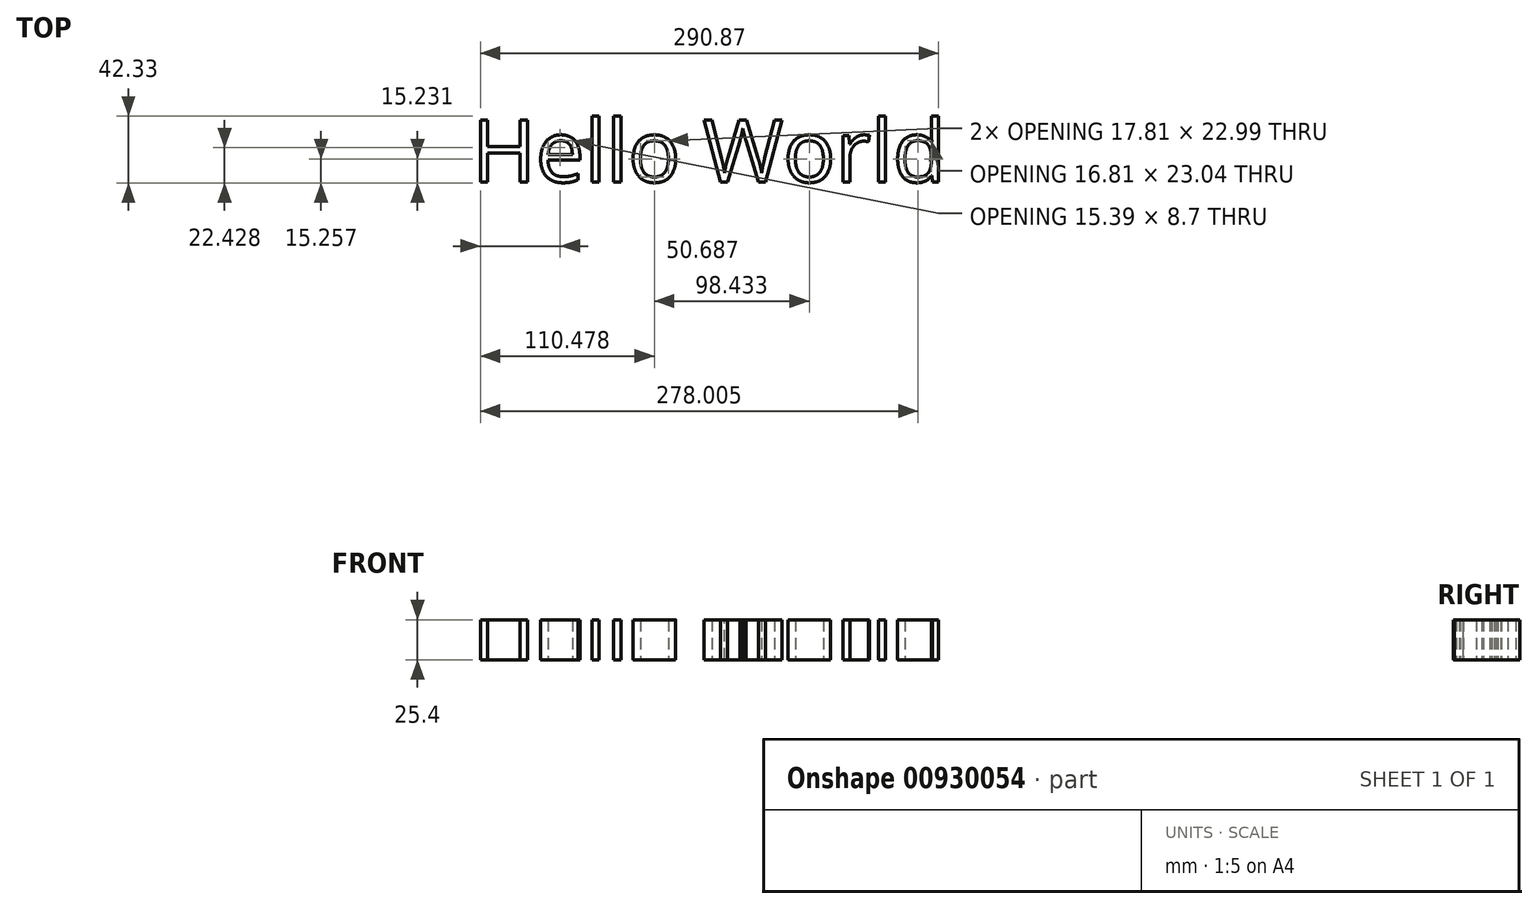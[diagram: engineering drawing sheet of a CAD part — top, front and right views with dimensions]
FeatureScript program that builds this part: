
annotation { "Feature Type Name" : "Feature", "Feature Type Description" : "" }
export const myFeature = defineFeature(function(context is Context, id is Id, definition is map)
    precondition{}
    {
        {
            var Q0;
            Q0=qCreatedBy(makeId("Top.planeOp"),FACE);
            var sketch = newSketch(context, id + "F0", { "sketchPlane" : qUnion([Q0])});
            skText(sketch, "E0", { "text": "Hello World", "fontName": "OpenSans-Regular.ttf"});
            const initialGuessF0  = {"E0": [0, 0, 1, 0, 0.0396]};
            skSetInitialGuess(sketch, initialGuessF0);
            skSolve(sketch);
        }
        {
            var Q0;
            Q0 = qSketchRegion(id + "F0", true);
            extrude(context, id + "F1", {"entities" : qUnion([Q0]), "depth" : 25.4 * mm, "offsetDistance" : 25.4 * mm});
        }
    });
